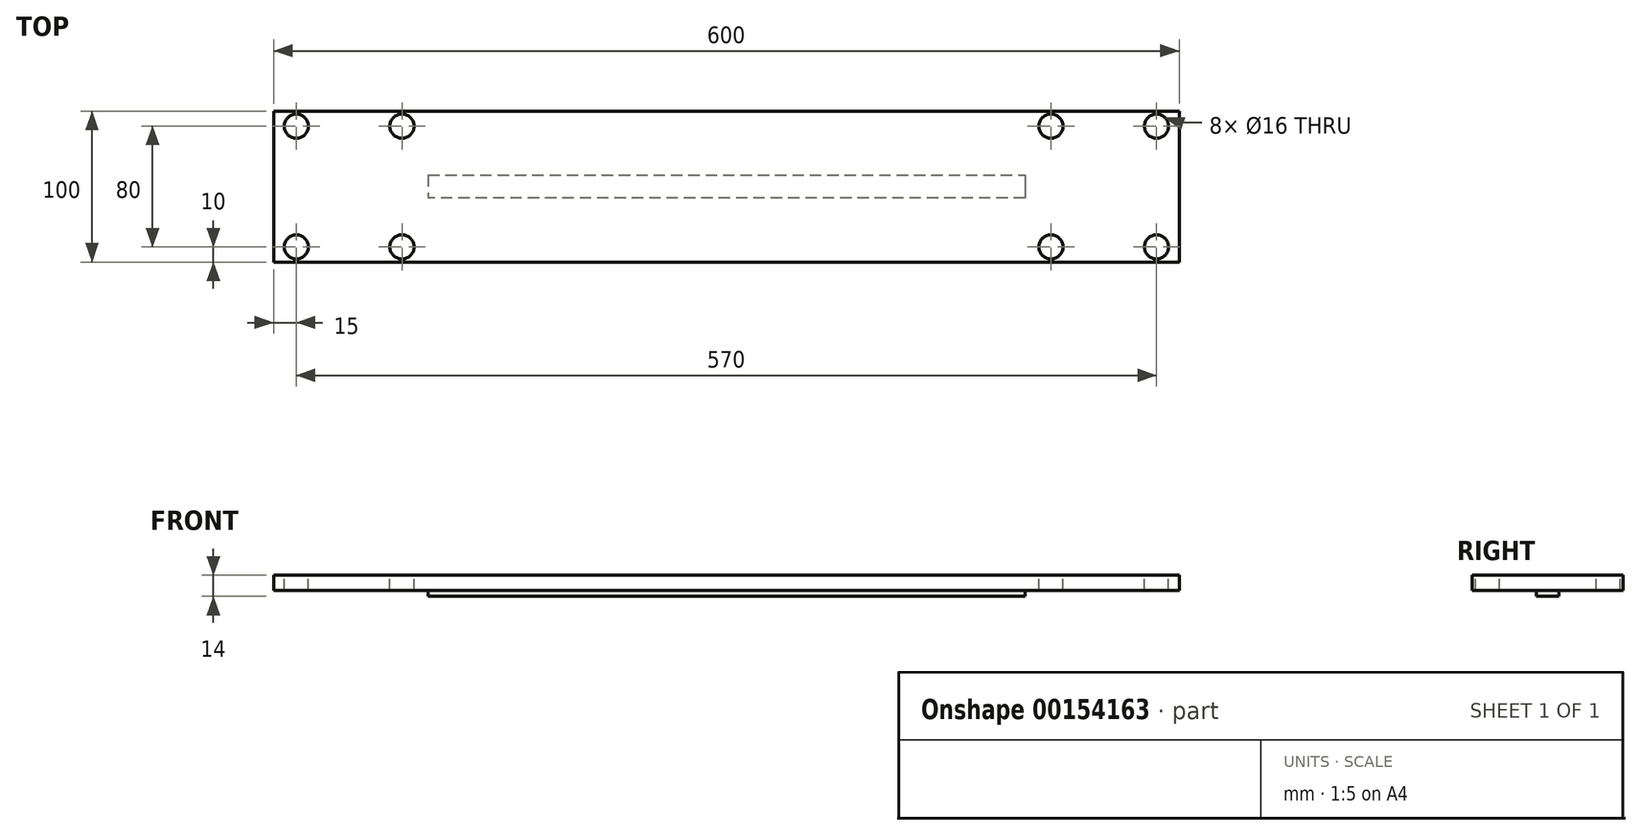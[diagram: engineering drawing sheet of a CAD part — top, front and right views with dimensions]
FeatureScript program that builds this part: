
annotation { "Feature Type Name" : "Feature", "Feature Type Description" : "" }
export const myFeature = defineFeature(function(context is Context, id is Id, definition is map)
    precondition{}
    {
        {
            var Q0;
            Q0=qCreatedBy(makeId("Front.planeOp"),FACE);
            var sketch = newSketch(context, id + "F0", { "sketchPlane" : qUnion([Q0])});
            skLineSegment(sketch, "E0", {"start": v(0, 0) * mm, "end": v(600, 0) * mm});
            skLineSegment(sketch, "E1", {"start": v(600, 0) * mm, "end": v(600, -10) * mm});
            skLineSegment(sketch, "E2", {"start": v(600, -10) * mm, "end": v(530, -10) * mm});
            skLineSegment(sketch, "E3", {"start": v(0, -10) * mm, "end": v(0, 0) * mm});
            skLineSegment(sketch, "E4", {"start": v(0, -10) * mm, "end": v(70, -10) * mm, "construction": true});
            skLineSegment(sketch, "E5", {"start": v(600, -10) * mm, "end": v(530, -10) * mm, "construction": true});
            skLineSegment(sketch, "E6.trimOffspring", {"start": v(70, -10) * mm, "end": v(0, -10) * mm});
            skLineSegment(sketch, "E7", {"start": v(70, -10) * mm, "end": v(530, -10) * mm});
            skSolve(sketch);
        }
        {
            var Q0;
            Q0 = qSketchRegion(id + "F0", true);
            extrude(context, id + "F1", {"entities" : qUnion([Q0]), "depth" : 100 * mm});
        }
        {
            var Q0;
            Q0=makeQuery(id+"F1.opExtrude","SWEPT_FACE",FACE,{"disambiguationData":[OSD([sQuery(id+"F0.wireOp",EDGE,"E0")])]});
            var sketch = newSketch(context, id + "F2", { "sketchPlane" : qUnion([Q0])});
            skLineSegment(sketch, "E8", {"start": v(0, -50) * mm, "end": v(100, -50) * mm, "construction": true});
            skLineSegment(sketch, "E9.bottom", {"start": v(85, -90) * mm, "end": v(15, -90) * mm});
            skLineSegment(sketch, "E9.top", {"start": v(85, -10) * mm, "end": v(15, -10) * mm});
            skLineSegment(sketch, "E9.left", {"start": v(85, -90) * mm, "end": v(85, -10) * mm});
            skLineSegment(sketch, "E9.right", {"start": v(15, -90) * mm, "end": v(15, -10) * mm});
            skPoint(sketch, "E9.middle", {"position": v(50, -50) * mm});
            skLineSegment(sketch, "E10", {"start": v(600, -50) * mm, "end": v(500, -50) * mm, "construction": true});
            skLineSegment(sketch, "E11.bottom", {"start": v(585, -90) * mm, "end": v(515, -90) * mm});
            skLineSegment(sketch, "E11.top", {"start": v(585, -10) * mm, "end": v(515, -10) * mm});
            skLineSegment(sketch, "E11.left", {"start": v(585, -90) * mm, "end": v(585, -10) * mm});
            skLineSegment(sketch, "E11.right", {"start": v(515, -90) * mm, "end": v(515, -10) * mm});
            skPoint(sketch, "E11.middle", {"position": v(550, -50) * mm});
            skSolve(sketch);
        }
        {
            var Q0;
            Q0=sQuery(id+"F2.wireOp",VERTEX,"E9.top.end");
            var Q1;
            Q1=sQuery(id+"F2.wireOp",VERTEX,"E9.bottom.end");
            var Q2;
            Q2=sQuery(id+"F2.wireOp",VERTEX,"E9.top.start");
            var Q3;
            Q3=sQuery(id+"F2.wireOp",VERTEX,"E9.left.start");
            var Q4;
            Q4=sQuery(id+"F2.wireOp",VERTEX,"E11.top.end");
            var Q5;
            Q5=sQuery(id+"F2.wireOp",VERTEX,"E11.right.start");
            var Q6;
            Q6=sQuery(id+"F2.wireOp",VERTEX,"E11.left.start");
            var Q7;
            Q7=sQuery(id+"F2.wireOp",VERTEX,"E11.left.end");
            var Q8;
            Q8=makeQuery(id+"F1.opExtrude","SWEPT_BODY",BODY,{"disambiguationData":[OSD([sQuery(id+"F0.wireOp",EDGE,"E0"),sQuery(id+"F0.wireOp",EDGE,"E1"),sQuery(id+"F0.wireOp",EDGE,"E2"),sQuery(id+"F0.wireOp",EDGE,"E3"),sQuery(id+"F0.wireOp",EDGE,"7ojeD2Lx-nS1t-1hTE-gq8g-C9srDyLe6pUy"),sQuery(id+"F0.wireOp",EDGE,"rq3Mynzp-fh6F-mfEs-RFJS-R7UwMkgZCplj"),sQuery(id+"F0.wireOp",EDGE,"qSBE7008-Ep3j-znpi-jIoY-ObV4W3xdA1eV"),sQuery(id+"F0.wireOp",EDGE,"E6.trimOffspring")])]});
            hole(context, id + "F3", {"style" : HoleStyle.SIMPLE, "endStyle" : HoleEndStyle.THROUGH, "holeDiameter" : 16 * mm, "locations" : qUnion([Q0, Q1, Q2, Q3, Q4, Q5, Q6, Q7]), "scope" : qUnion([Q8]), "isTappedThrough" : true});
        }
        {
            var Q0;
            Q0=makeQuery(id+"F1.opExtrude","SWEPT_FACE",FACE,{"disambiguationData":[OSD([sQuery(id+"F0.wireOp",EDGE,"E2"),sQuery(id+"F0.wireOp",EDGE,"E6.trimOffspring"),sQuery(id+"F0.wireOp",EDGE,"E7")])]});
            var sketch = newSketch(context, id + "F4", { "sketchPlane" : qUnion([Q0])});
            skLineSegment(sketch, "E12", {"start": v(0, 50) * mm, "end": v(600, 50) * mm, "construction": true});
            skLineSegment(sketch, "E13", {"start": v(93, 90.34) * mm, "end": v(102.3, 90.34) * mm, "construction": true});
            skLineSegment(sketch, "E14", {"start": v(102.3, 90.34) * mm, "end": v(102.3, 50) * mm, "construction": true});
            skLineSegment(sketch, "E15", {"start": v(507, 89.78) * mm, "end": v(497.7, 89.75) * mm, "construction": true});
            skLineSegment(sketch, "E16", {"start": v(497.7, 89.75) * mm, "end": v(497.85, 50) * mm, "construction": true});
            skLineSegment(sketch, "E17", {"start": v(102.3, 50) * mm, "end": v(102.3, 57.5) * mm});
            skLineSegment(sketch, "E18", {"start": v(102.3, 50) * mm, "end": v(102.3, 42.5) * mm});
            skLineSegment(sketch, "E19", {"start": v(102.3, 42.5) * mm, "end": v(497.85, 42.5) * mm});
            skLineSegment(sketch, "E20", {"start": v(497.85, 42.5) * mm, "end": v(497.85, 50) * mm});
            skLineSegment(sketch, "E21", {"start": v(497.85, 50) * mm, "end": v(497.83, 57.5) * mm});
            skLineSegment(sketch, "E22", {"start": v(497.83, 57.5) * mm, "end": v(102.3, 57.5) * mm});
            skSolve(sketch);
        }
        {
            var Q0;
            Q0 = qSketchRegion(id + "F4", true);
            extrude(context, id + "F5", {"entities" : qUnion([Q0]), "operationType" : NewBodyOperationType.ADD, "depth" : 4 * mm});
        }
    });
